# Revit family: Lighting_Ceiling-Mounted_Nordlux_Alba-Pro_30
name_source: partatom
category: Lighting Fixtures
revit_build: Autodesk Revit 2017 (Build: 20160225_1515(x64)
units: mm (PartAtom-declared; Revit-internal decimal feet)

## family parameters
Always vertical = Yes
Cut with Voids When Loaded = No
Host = Ceiling
Light Source = Yes
OmniClass Number = 23.80.70.11
OmniClass Title = Luminaries for Internal Lighting
Part Type = Normal
Room Calculation Point = No
Round Connector Dimension = Use Diameter
Shared = No

## types (1)
- Alba Pro 30
    ArticleNumber = 77176001
    AssetType = Fixed
    BIMObjectName = Lighting_Ceiling-Mounted_Nordlux_Alba-Pro_30
    Brand = Nordlux
    Category = Indoor lighting
    Collection = Alba Pro
    Color = White
    Color Filter = 16777215
    ColourIndexRA = 80
    ConvergoRefNr = 0143-1909-0020-DK
    DefaultElevation = 0 mm  [stored 0 ft]
    Description = With Alba Pro, Bonnelycke MDD has created a ceiling fixture that breaks with tradition. A ceiling fixture where design and innovation merge into something greater. The shape stands out as sharp, modern and as a uniform, luminous surface. The functional kip joint, made from brass, adds an elegant superiority to the design.
    Designer = Bonnelycke MDD
    Dimmer = Dimmable
    Dimming Lamp Color Temperature Shift = <None>
    DurationUnit = Hours
    EANNumber = 5701581400382
    ElectricalDeviceNominalPower = 0
    Emit Shape Visible in Rendering = No
    Emit from Circle Diameter = 290 mm  [stored 0.951444 ft]
    EnergyClass = A++ - A
    ExpectedLife = 20.000
    Finish = Primary material aluminium, secondary material acrylic.
    HasProtectiveEarth = No
    IP_Code = IP20
    IfcExportAs = IfcLightFixtureType
    IfcExportType = NOTDEFINED
    InsulationStandardClass = Class 2 (Double isolated)
    LensMaterial = Opal white
    LightFixtureMainMaterial = White
    LightFixtureMountingType = Surface
    LightFixturePlacingType = Ceilling
    LightSource = Incl. 14W LED
    MaintenanceFactor = 0
    Manufacturer = Nordlux
    ManufacturerName = Nordlux
    ManufacturerURL = https://www.nordlux.com
    Material = Aluminium & acrylic
    Model = Alba Pro 30
    ModelReference = 77176001
    NBSDescription = General purpose luminaires
    NBSReference = 90-60-50/405
    Name = Alba-Pro_30
    NominalCurrent = 0 A
    NominalDiameter = 300 mm  [stored 0.984252 ft]
    NominalFrequencyRange = 50 Hz
    NominalHeight = 100 mm  [stored 0.328084 ft]
    NominalLength = 300 mm  [stored 0.984252 ft]
    NominalRadius = 150 mm  [stored 0.492126 ft]
    NominalVoltage = 230 V
    NominalVoltageCalc = 0 V
    NominalWidth = 300 mm  [stored 0.984252 ft]
    NumberOfPoles = 1
    NumberOfSources = 0
    PhaseAngle = 0.00°
    Photometric Web File = 7717 Alba Pro 30.ies
    Product data url = https://www.bimobject.com
    Revision = 1
    Shape = Sculptured
    Size = 300x300x100 mm
    Socket = LED MODUL
    Tilt Angle = 90.00°
    TotalWattage = 14 W
    URL = https://www.nordlux.com
    Uniclass2 = Pr_70_70_49_43
    Uniclass2015Description = Light-Emitting Diode (LED) Luminaires
    Uniclass2015Reference = Pr_70_70_48_46
    UsageCurrent = 0 A
    Version = 1
    VersionDate = 01/07/2020
    WarrantyDurationUnit = Hours

note: [stored X ft] marks values corroborated as IEEE doubles in the binary element streams (Revit-internal decimal feet)

## geometry (parser evidence)
native form markers: Sweep x6
no freeform markers — native parametric forms only
